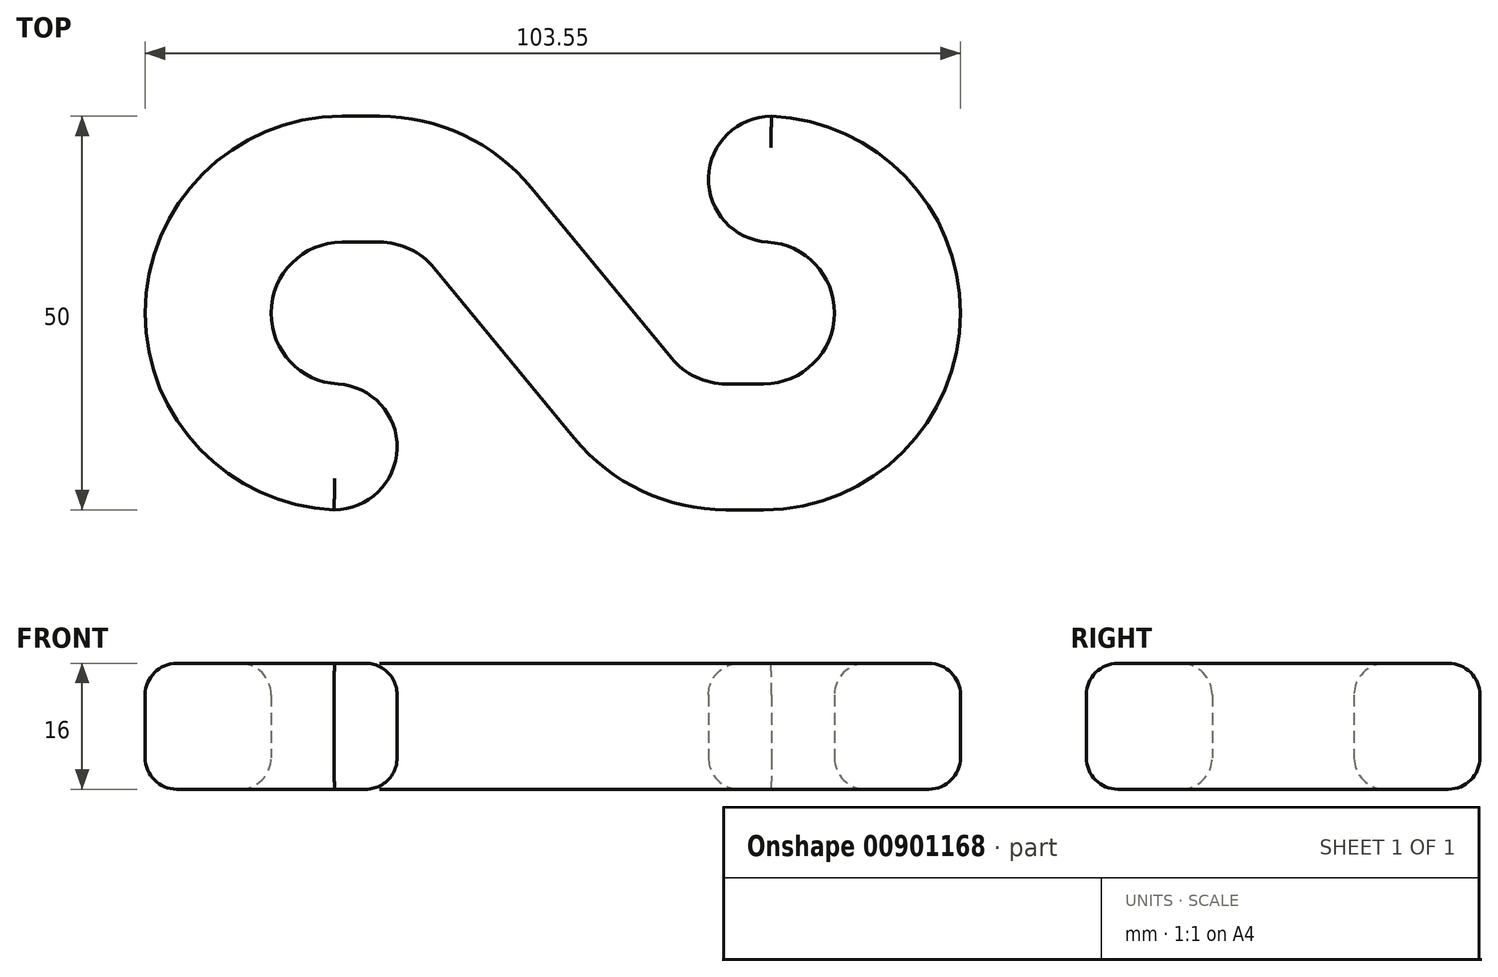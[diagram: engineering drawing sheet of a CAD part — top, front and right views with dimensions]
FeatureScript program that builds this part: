
annotation { "Feature Type Name" : "Feature", "Feature Type Description" : "" }
export const myFeature = defineFeature(function(context is Context, id is Id, definition is map)
    precondition{}
    {
        {
            var Q0;
            Q0=qCreatedBy(makeId("Top.planeOp"),FACE);
            var sketch = newSketch(context, id + "F0", { "sketchPlane" : qUnion([Q0])});
            skLineSegment(sketch, "E0", {"start": v(103.55, 0) * mm, "end": v(103.55, 50) * mm});
            skLineSegment(sketch, "E1", {"start": v(103.55, 50) * mm, "end": v(71.55, 50) * mm});
            skLineSegment(sketch, "E2", {"start": v(0, 50) * mm, "end": v(0, 0) * mm});
            skLineSegment(sketch, "E3", {"start": v(71.55, 34) * mm, "end": v(87.55, 34) * mm});
            skLineSegment(sketch, "E4", {"start": v(71.55, 50) * mm, "end": v(71.55, 34) * mm});
            skLineSegment(sketch, "E5", {"start": v(0, 0) * mm, "end": v(32, 0) * mm});
            skLineSegment(sketch, "E6", {"start": v(32, 0) * mm, "end": v(32, 16) * mm});
            skLineSegment(sketch, "E7", {"start": v(32, 16) * mm, "end": v(16, 16) * mm});
            skLineSegment(sketch, "E8", {"start": v(16, 16) * mm, "end": v(16, 34) * mm});
            skLineSegment(sketch, "E9", {"start": v(87.55, 34) * mm, "end": v(87.55, 16) * mm});
            skLineSegment(sketch, "E10", {"start": v(16, 34) * mm, "end": v(34, 34) * mm});
            skLineSegment(sketch, "E11", {"start": v(0, 50) * mm, "end": v(41.55, 50) * mm});
            skLineSegment(sketch, "E12", {"start": v(34, 34) * mm, "end": v(62, 0) * mm});
            skLineSegment(sketch, "E13", {"start": v(41.55, 50) * mm, "end": v(69.55, 16) * mm});
            skLineSegment(sketch, "E14", {"start": v(87.55, 16) * mm, "end": v(69.55, 16) * mm});
            skLineSegment(sketch, "E15", {"start": v(103.55, 0) * mm, "end": v(62, 0) * mm});
            skSolve(sketch);
        }
        {
            var Q0;
            Q0=makeQuery(id+"F0.imprint","IMPRINT",FACE,{"disambiguationData":[TD([[makeQuery(id+"F0.imprint","IMPRINT",EDGE,{"derivedFrom":sQuery(id+"F0.wireOp",EDGE,"E0")}),1.0]])]});
            extrude(context, id + "F1", {"entities" : qUnion([Q0]), "depth" : 16 * mm, "offsetDistance" : 25 * mm});
        }
        {
            var Q0;
            Q0=makeQuery(id+"F1.opExtrude","SWEPT_EDGE",EDGE,{"disambiguationData":[OSD([sQuery(id+"F0.wireOp",EDGE,"E5"),sQuery(id+"F0.wireOp",EDGE,"E6")])]});
            var Q1;
            Q1=makeQuery(id+"F1.opExtrude","SWEPT_EDGE",EDGE,{"disambiguationData":[OSD([sQuery(id+"F0.wireOp",EDGE,"E6"),sQuery(id+"F0.wireOp",EDGE,"E7")])]});
            var Q2;
            Q2=makeQuery(id+"F1.opExtrude","SWEPT_EDGE",EDGE,{"disambiguationData":[OSD([sQuery(id+"F0.wireOp",EDGE,"E3"),sQuery(id+"F0.wireOp",EDGE,"E4")])]});
            var Q3;
            Q3=makeQuery(id+"F1.opExtrude","SWEPT_EDGE",EDGE,{"disambiguationData":[OSD([sQuery(id+"F0.wireOp",EDGE,"E1"),sQuery(id+"F0.wireOp",EDGE,"E4")])]});
            fillet(context, id + "F2", {"entities" : qUnion([Q0, Q1, Q2, Q3]), "radius" : 8 * mm, "tangentPropagation" : true, "allowEdgeOverflow" : false});
        }
        {
            var Q0;
            Q0=makeQuery(id+"F1.opExtrude","SWEPT_EDGE",EDGE,{"disambiguationData":[OSD([sQuery(id+"F0.wireOp",EDGE,"E3"),sQuery(id+"F0.wireOp",EDGE,"E9")])]});
            var Q1;
            Q1=makeQuery(id+"F1.opExtrude","SWEPT_EDGE",EDGE,{"disambiguationData":[OSD([sQuery(id+"F0.wireOp",EDGE,"E9"),sQuery(id+"F0.wireOp",EDGE,"E14")])]});
            var Q2;
            Q2=makeQuery(id+"F1.opExtrude","SWEPT_EDGE",EDGE,{"disambiguationData":[OSD([sQuery(id+"F0.wireOp",EDGE,"E13"),sQuery(id+"F0.wireOp",EDGE,"E14")])]});
            var Q3;
            Q3=makeQuery(id+"F1.opExtrude","SWEPT_EDGE",EDGE,{"disambiguationData":[OSD([sQuery(id+"F0.wireOp",EDGE,"E8"),sQuery(id+"F0.wireOp",EDGE,"E10")])]});
            var Q4;
            Q4=makeQuery(id+"F1.opExtrude","SWEPT_EDGE",EDGE,{"disambiguationData":[OSD([sQuery(id+"F0.wireOp",EDGE,"E10"),sQuery(id+"F0.wireOp",EDGE,"E12")])]});
            var Q5;
            Q5=makeQuery(id+"F1.opExtrude","SWEPT_EDGE",EDGE,{"disambiguationData":[OSD([sQuery(id+"F0.wireOp",EDGE,"E7"),sQuery(id+"F0.wireOp",EDGE,"E8")])]});
            fillet(context, id + "F3", {"entities" : qUnion([Q0, Q1, Q2, Q3, Q4, Q5]), "radius" : 9 * mm, "tangentPropagation" : true, "allowEdgeOverflow" : false});
        }
        {
            var Q0;
            Q0=makeQuery(id+"F1.opExtrude","SWEPT_EDGE",EDGE,{"disambiguationData":[OSD([sQuery(id+"F0.wireOp",EDGE,"E0"),sQuery(id+"F0.wireOp",EDGE,"E1")])]});
            var Q1;
            Q1=makeQuery(id+"F1.opExtrude","SWEPT_EDGE",EDGE,{"disambiguationData":[OSD([sQuery(id+"F0.wireOp",EDGE,"E0"),sQuery(id+"F0.wireOp",EDGE,"E15")])]});
            var Q2;
            Q2=makeQuery(id+"F1.opExtrude","SWEPT_EDGE",EDGE,{"disambiguationData":[OSD([sQuery(id+"F0.wireOp",EDGE,"E2"),sQuery(id+"F0.wireOp",EDGE,"E5")])]});
            var Q3;
            Q3=makeQuery(id+"F1.opExtrude","SWEPT_EDGE",EDGE,{"disambiguationData":[OSD([sQuery(id+"F0.wireOp",EDGE,"E2"),sQuery(id+"F0.wireOp",EDGE,"E11")])]});
            var Q4;
            Q4=makeQuery(id+"F1.opExtrude","SWEPT_EDGE",EDGE,{"disambiguationData":[OSD([sQuery(id+"F0.wireOp",EDGE,"E12"),sQuery(id+"F0.wireOp",EDGE,"E15")])]});
            var Q5;
            Q5=makeQuery(id+"F1.opExtrude","SWEPT_EDGE",EDGE,{"disambiguationData":[OSD([sQuery(id+"F0.wireOp",EDGE,"E11"),sQuery(id+"F0.wireOp",EDGE,"E13")])]});
            fillet(context, id + "F4", {"entities" : qUnion([Q0, Q1, Q2, Q3, Q4, Q5]), "radius" : 25 * mm, "tangentPropagation" : true, "allowEdgeOverflow" : false});
        }
        {
            var Q0;
            Q0=makeQuery(id+"F1.opExtrude","CAP_FACE",FACE,{"disambiguationData":[OSD([sQuery(id+"F0.wireOp",EDGE,"E0"),sQuery(id+"F0.wireOp",EDGE,"E1"),sQuery(id+"F0.wireOp",EDGE,"E2"),sQuery(id+"F0.wireOp",EDGE,"E3"),sQuery(id+"F0.wireOp",EDGE,"E4"),sQuery(id+"F0.wireOp",EDGE,"E5"),sQuery(id+"F0.wireOp",EDGE,"E6"),sQuery(id+"F0.wireOp",EDGE,"E7"),sQuery(id+"F0.wireOp",EDGE,"E8"),sQuery(id+"F0.wireOp",EDGE,"E9"),sQuery(id+"F0.wireOp",EDGE,"E10"),sQuery(id+"F0.wireOp",EDGE,"E11"),sQuery(id+"F0.wireOp",EDGE,"E12"),sQuery(id+"F0.wireOp",EDGE,"E13"),sQuery(id+"F0.wireOp",EDGE,"E14"),sQuery(id+"F0.wireOp",EDGE,"E15")])],"isStart":false});
            var Q1;
            Q1=makeQuery(id+"F1.opExtrude","CAP_FACE",FACE,{"disambiguationData":[OSD([sQuery(id+"F0.wireOp",EDGE,"E0"),sQuery(id+"F0.wireOp",EDGE,"E1"),sQuery(id+"F0.wireOp",EDGE,"E2"),sQuery(id+"F0.wireOp",EDGE,"E3"),sQuery(id+"F0.wireOp",EDGE,"E4"),sQuery(id+"F0.wireOp",EDGE,"E5"),sQuery(id+"F0.wireOp",EDGE,"E6"),sQuery(id+"F0.wireOp",EDGE,"E7"),sQuery(id+"F0.wireOp",EDGE,"E8"),sQuery(id+"F0.wireOp",EDGE,"E9"),sQuery(id+"F0.wireOp",EDGE,"E10"),sQuery(id+"F0.wireOp",EDGE,"E11"),sQuery(id+"F0.wireOp",EDGE,"E12"),sQuery(id+"F0.wireOp",EDGE,"E13"),sQuery(id+"F0.wireOp",EDGE,"E14"),sQuery(id+"F0.wireOp",EDGE,"E15")])],"isStart":true});
            fillet(context, id + "F5", {"entities" : qUnion([Q0, Q1]), "radius" : 4 * mm, "tangentPropagation" : true, "allowEdgeOverflow" : false});
        }
    });
